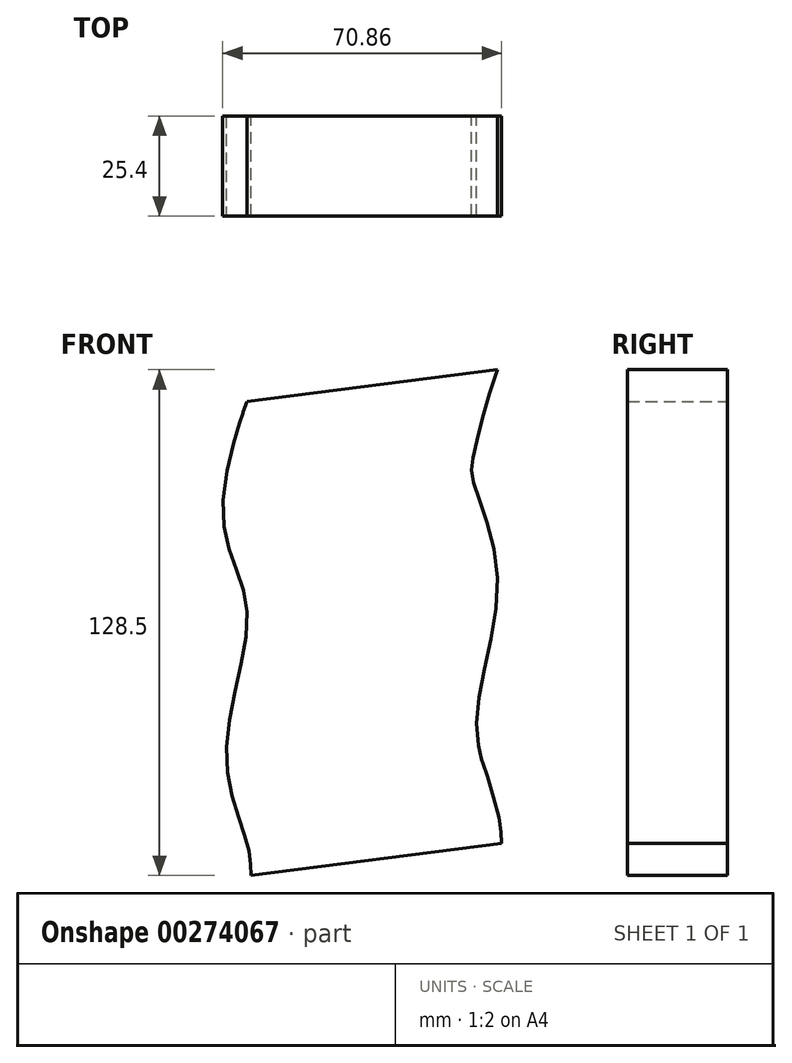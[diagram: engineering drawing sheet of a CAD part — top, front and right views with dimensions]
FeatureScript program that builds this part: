
annotation { "Feature Type Name" : "Feature", "Feature Type Description" : "" }
export const myFeature = defineFeature(function(context is Context, id is Id, definition is map)
    precondition{}
    {
        {
            var Q0;
            Q0=qCreatedBy(makeId("Front.planeOp"),FACE);
            var sketch = newSketch(context, id + "F0", { "sketchPlane" : qUnion([Q0])});
            skFitSpline(sketch, "E0", {"points": [v(-27.66, -59.3) * mm, v(-28.7, -51.17) * mm, v(-34, -28.12) * mm, v(-28.7, 8.2) * mm, v(-34.88, 32.77) * mm, v(-29.73, 58.23) * mm, v(-29.7, 58.34) * mm, v(-29.69, 58.36) * mm, v(-29.68, 58.37) * mm, v(-28.7, 61.07) * mm], "startDerivative": vector(-2.13, 61.36) * mm, "endDerivative": vector(48.17, 131.92) * mm});
            skFitSpline(sketch, "E1", {"points": [v(35.97, -51.17) * mm, v(34.94, -43.04) * mm, v(31.15, -30.62) * mm, v(31.12, -30.54) * mm, v(29.63, -19.99) * mm, v(34.94, 16.32) * mm, v(28.75, 40.9) * mm, v(28.77, 47.28) * mm, v(34.94, 69.2) * mm], "startDerivative": vector(-2.13, 61.36) * mm, "endDerivative": vector(48.17, 131.92) * mm});
            skLineSegment(sketch, "E2", {"start": v(-27.66, -59.3) * mm, "end": v(35.97, -51.17) * mm});
            skLineSegment(sketch, "E3", {"start": v(34.94, 69.2) * mm, "end": v(-28.7, 61.07) * mm});
            skSolve(sketch);
        }
        {
            var Q0;
            Q0=makeQuery(id+"F0.imprint","IMPRINT",FACE,{"disambiguationData":[TD([[makeQuery(id+"F0.imprint","IMPRINT",EDGE,{"derivedFrom":sQuery(id+"F0.wireOp",EDGE,"E0")}),-1.0]])]});
            extrude(context, id + "F1", {"entities" : qUnion([Q0]), "depth" : 25.4 * mm});
        }
        {
            var Q0;
            Q0=makeQuery(id+"F1.opExtrude","CAP_FACE",FACE,{"disambiguationData":[OSD([sQuery(id+"F0.wireOp",EDGE,"E0"),sQuery(id+"F0.wireOp",EDGE,"E1"),sQuery(id+"F0.wireOp",EDGE,"E2"),sQuery(id+"F0.wireOp",EDGE,"E3")])],"isStart":true});
            var sketch = newSketch(context, id + "F2", { "sketchPlane" : qUnion([Q0])});
            skLineSegment(sketch, "E4", {"start": v(-23.86, 0) * mm, "end": v(-23.86, 25.16) * mm});
            skLineSegment(sketch, "E5", {"start": v(-23.86, 25.16) * mm, "end": v(-22, 38.37) * mm});
            skLineSegment(sketch, "E6", {"start": v(-22, 38.37) * mm, "end": v(-23.86, 60.44) * mm});
            skLineSegment(sketch, "E7", {"start": v(-23.86, 60.44) * mm, "end": v(-2.87, 58.58) * mm});
            skLineSegment(sketch, "E8", {"start": v(-2.87, 58.58) * mm, "end": v(23.09, 55.94) * mm});
            skLineSegment(sketch, "E9", {"start": v(23.09, 55.94) * mm, "end": v(26.2, 41.01) * mm});
            skLineSegment(sketch, "E10", {"start": v(26.2, 41.01) * mm, "end": v(21.22, 14.28) * mm});
            skLineSegment(sketch, "E11", {"start": v(21.22, 14.28) * mm, "end": v(23.4, -10.6) * mm});
            skLineSegment(sketch, "E12", {"start": v(23.4, -10.6) * mm, "end": v(27.44, -34.07) * mm});
            skLineSegment(sketch, "E13", {"start": v(27.44, -34.07) * mm, "end": v(22.15, -52.4) * mm});
            skLineSegment(sketch, "E14", {"start": v(22.15, -52.4) * mm, "end": v(-25.26, -46.5) * mm});
            skLineSegment(sketch, "E15", {"start": v(-25.26, -46.5) * mm, "end": v(-20.28, -28.32) * mm});
            skLineSegment(sketch, "E16", {"start": v(-20.28, -28.32) * mm, "end": v(-23.86, 0) * mm});
            skPoint(sketch, "E17", {"position": v(-23.86, 3.55) * mm});
            skSolve(sketch);
        }
    });
